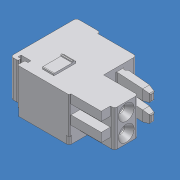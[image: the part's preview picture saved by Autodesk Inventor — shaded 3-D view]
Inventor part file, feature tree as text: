
AUTODESK INVENTOR PART (.ipt)
format: ipt  version: unknown  size: 426,496 bytes
history: native  units: mm (DEFAULTED — no unit token found)
features: sketch x20, extrude x19, pattern_linear x6, revolve x1
ambient origin geometry x8: Origin, YZ Plane, XZ Plane, XY Plane, X Axis, Y Axis, Z Axis, Center Point
feature tree (46):
  extrude  "Extrusion1"  Depth=1.5mm TaperAngle=0.0deg
  extrude  "Extrusion2"  Depth=1.5mm TaperAngle=0.0deg
  extrude  "Extrusion3"  Depth=1.5mm TaperAngle=0.0deg
  extrude  "Extrusion4"  Depth=1.5mm TaperAngle=0.0deg
  extrude  "Extrusion5"  TaperAngle=360.0deg  [1 undecoded]
  extrude  "Extrusion6"  Depth=3.3mm TaperAngle=0.0deg
  extrude  "Extrusion7"  Depth=1.0mm TaperAngle=0.0deg
  extrude  "Extrusion8"  Depth=1.0mm TaperAngle=0.0deg
  extrude  "Extrusion9"  Depth=0.9mm TaperAngle=0.0deg
  revolve  "Revolution1"  [1 undecoded]
  pattern_linear  "Rectangular Pattern1"  Count1=2 Spacing1=3.5mm
  extrude  "Extrusion10"  Depth=20.0mm TaperAngle=0.0deg
  pattern_linear  "Rectangular Pattern2"  [2 undecoded]
  extrude  "Extrusion11"  [1 undecoded]
  pattern_linear  "Rectangular Pattern3"  [2 undecoded]
  extrude  "Extrusion12"  [1 undecoded]
  pattern_linear  "Rectangular Pattern4"  [2 undecoded]
  extrude  "Extrusion13"  [1 undecoded]
  extrude  "Extrusion14"  [1 undecoded]
  extrude  "Extrusion15"  [1 undecoded]
  extrude  "Extrusion16"  [1 undecoded]
  extrude  "Extrusion17"  [1 undecoded]
  pattern_linear  "Rectangular Pattern5"  [2 undecoded]
  extrude  "Extrusion18"  [1 undecoded]
  pattern_linear  "Rectangular Pattern6"  [2 undecoded]
  extrude  "Extrusion19"  [1 undecoded]
  sketch  "Skizze_1"  dims[d0=7.0mm d1=0.0mm d2=1.5mm d3=0.0mm]
  sketch  "Skizze_3"  dims[d8=1.5mm d9=0.0mm d10=1.5mm d11=0.0mm]
  sketch  "Skizze_4"  dims[d12=1.5mm d13=0.0mm d14=1.5mm d15=0.0mm]
  sketch  "Skizze_5"  dims[d16=1.4mm d17=0.0mm d18=360.0deg]
  sketch  "Skizze_6"  dims[d19=20.0mm d21=3.5mm d22=10.0mm d24=0.0mm d25=3.3mm d26=0.0mm]
  sketch  "Skizze_7"  dims[d27=20.0mm d29=3.5mm d30=10.0mm d32=0.0mm d33=1.0mm d34=0.0mm]
  sketch  "Skizze_8"  dims[d35=20.0mm d37=3.5mm d38=10.0mm d40=0.0mm d41=1.0mm d42=0.0mm]
  sketch  "Skizze_9"  dims[d43=20.0mm d45=3.5mm d46=10.0mm d48=0.0mm d49=0.9mm d50=0.0mm]
  sketch  "Skizze_2"  dims[d4=1.5mm d5=0.0mm d6=1.5mm d7=0.0mm]
  sketch  "Skizze_10"  dims[d51=0.9mm d52=0.0mm d53=1.7mm d54=0.0mm]
  sketch  "Skizze_12"  dims[d55=1.7mm d56=0.0mm]
  sketch  "Skizze_14"  dims[d57=2.0mm d58=0.0mm d59=20.0mm d61=3.5mm d62=10.0mm d64=0.0mm]
  sketch  "Skizze_16"  dims[d65=1.7mm d66=0.0mm d67=20.0mm d69=3.5mm d70=10.0mm d72=0.0mm]
  sketch  "Skizze_18"  dims[d73=2.2mm d74=0.0mm]
  sketch  "Skizze_19"
  sketch  "Skizze_20"
  sketch  "Skizze_21"
  sketch  "Skizze_22"
  sketch  "Skizze_24"
  sketch  "Skizze_26"
note: 21 required parameter values undecoded (feature->parameter linkage not recoverable at this tier; creation-order binding heuristic only, values carry confidence <= 0.55)